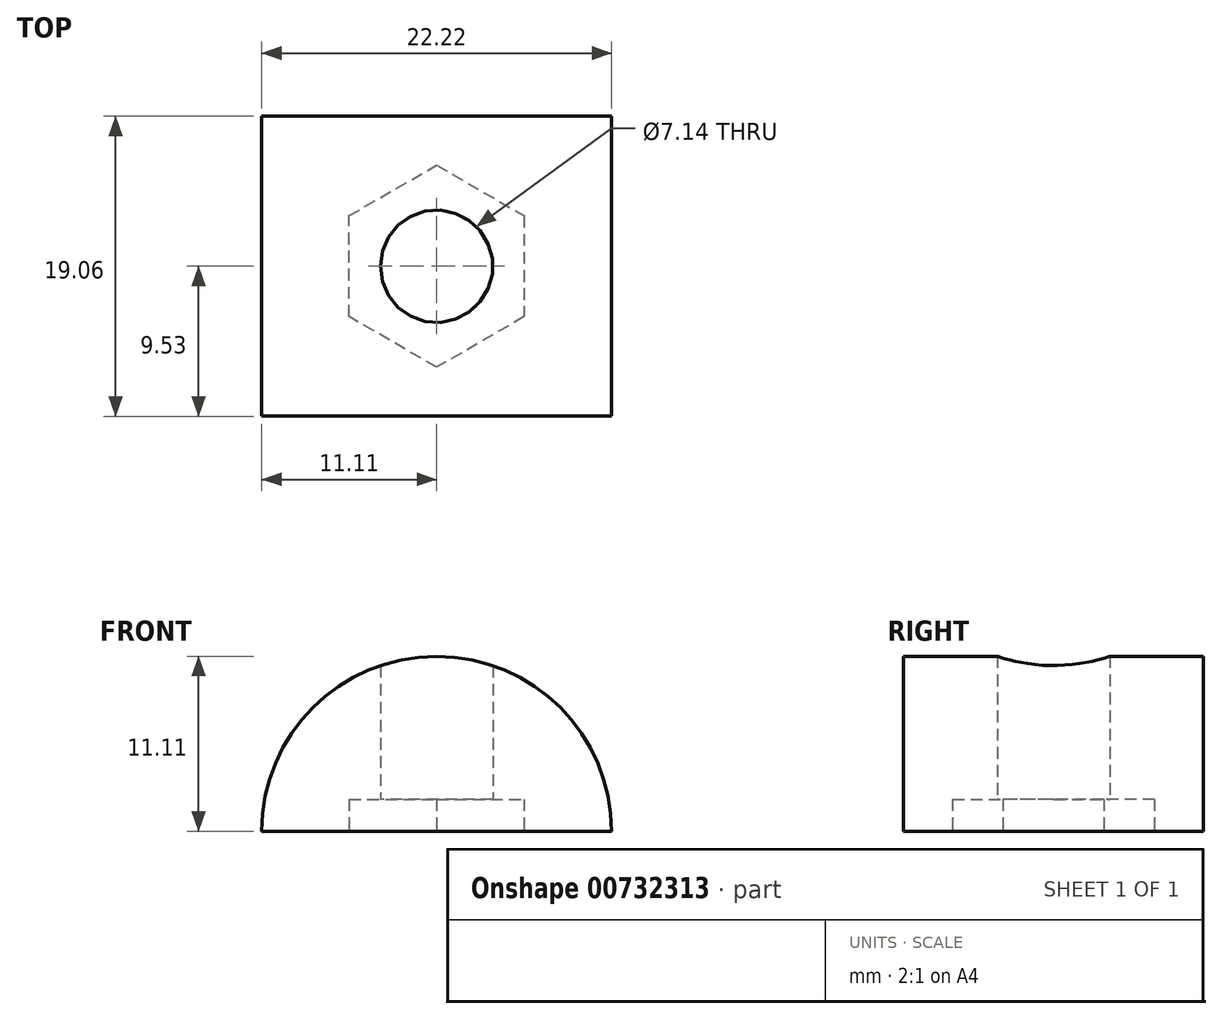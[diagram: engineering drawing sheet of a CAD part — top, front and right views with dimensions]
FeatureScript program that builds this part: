
annotation { "Feature Type Name" : "Feature", "Feature Type Description" : "" }
export const myFeature = defineFeature(function(context is Context, id is Id, definition is map)
    precondition{}
    {
        {
            var Q0;
            Q0=qCreatedBy(makeId("Top.planeOp"),FACE);
            var sketch = newSketch(context, id + "F0", { "sketchPlane" : qUnion([Q0])});
            skCircle(sketch, "E0.cCircle", {"center": v(0, 0) * mm, "radius": 5.56 * mm, "construction": true});
            skLineSegment(sketch, "E0.0", {"start": v(5.56, 3.2) * mm, "end": v(5.56, -3.2) * mm});
            skLineSegment(sketch, "E0.1", {"start": v(5.56, -3.2) * mm, "end": v(0, -6.42) * mm});
            skLineSegment(sketch, "E0.2", {"start": v(0, -6.42) * mm, "end": v(-5.56, -3.2) * mm});
            skLineSegment(sketch, "E0.3", {"start": v(-5.56, -3.2) * mm, "end": v(-5.56, 3.2) * mm});
            skLineSegment(sketch, "E0.4", {"start": v(-5.56, 3.2) * mm, "end": v(0, 6.42) * mm});
            skLineSegment(sketch, "E0.5", {"start": v(0, 6.42) * mm, "end": v(5.56, 3.2) * mm});
            skPoint(sketch, "E0.0.midPoint", {"position": v(5.56, 0) * mm});
            skCircle(sketch, "E1", {"center": v(0, 0) * mm, "radius": 3.57 * mm});
            skSolve(sketch);
        }
        {
            var Q0;
            Q0=qCreatedBy(makeId("Front.planeOp"),FACE);
            var sketch = newSketch(context, id + "F1", { "sketchPlane" : qUnion([Q0])});
            skArc(sketch, "E2", {"start": v(11.11, 0) * mm, "mid": v(0, 11.11) * mm, "end": v(-11.11, 0) * mm});
            skLineSegment(sketch, "E3", {"start": v(11.11, 0) * mm, "end": v(-11.11, 0) * mm});
            skSolve(sketch);
        }
        {
            var Q0;
            Q0=makeQuery(id+"F1.imprint","IMPRINT",FACE,{"disambiguationData":[TD([[makeQuery(id+"F1.imprint","IMPRINT",EDGE,{"derivedFrom":sQuery(id+"F1.wireOp",EDGE,"E2")}),1.0]])]});
            extrude(context, id + "F2", {"entities" : qUnion([Q0]), "endBound" : BoundingType.SYMMETRIC, "depth" : 19.05 * mm, "offsetDistance" : 25.4 * mm});
        }
        {
            var Q0;
            Q0=makeQuery(id+"F0.imprint","IMPRINT",FACE,{"disambiguationData":[TD([[makeQuery(id+"F0.imprint","IMPRINT",EDGE,{"derivedFrom":sQuery(id+"F0.wireOp",EDGE,"E0.0")}),-1.0]])]});
            extrude(context, id + "F3", {"entities" : qUnion([Q0]), "operationType" : NewBodyOperationType.REMOVE, "depth" : 2.03 * mm, "offsetDistance" : 25.4 * mm});
        }
        {
            var Q0;
            Q0=makeQuery(id+"F3.boolean.opBoolean","SPLIT",FACE,{"disambiguationData":[TD([makeQuery(id+"F3.opExtrude","SWEPT_FACE",FACE,{"disambiguationData":[OSD([sQuery(id+"F0.wireOp",EDGE,"E1")])]})])],"derivedFrom":makeQuery(id+"F2.opExtrude","SWEPT_FACE",FACE,{"disambiguationData":[OSD([sQuery(id+"F1.wireOp",EDGE,"E3")])]})});
            extrude(context, id + "F4", {"entities" : qUnion([Q0]), "operationType" : NewBodyOperationType.REMOVE, "oppositeDirection" : true, "depth" : 25.4 * mm, "offsetDistance" : 25.4 * mm});
        }
    });
